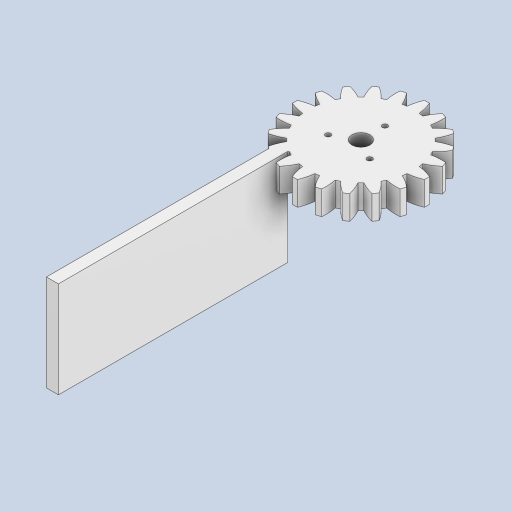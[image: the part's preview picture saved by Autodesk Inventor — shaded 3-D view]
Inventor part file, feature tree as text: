
AUTODESK INVENTOR PART (.ipt)
format: ipt  version: 2023 (Build 270158000, 158)  size: 265,216 bytes
history: native  units: mm (DEFAULTED — no unit token found)
features: sketch x5, extrude x4, plane x3, other x3
ambient origin geometry x8: Origin, YZ Plane, XZ Plane, XY Plane, X Axis, Y Axis, Z Axis, Center Point
bodies: Solid1 (feature_tree)
feature tree (15):
  extrude  "Extrusion1"  Depth=10.0mm TaperAngle=0.0deg
  plane  "Work Plane2"
  plane  "Work Plane8"
  plane  "Work Plane9"
  other  "平歯車"
  extrude  "押し出し2"  Depth=10.0mm TaperAngle=0.0deg
  extrude  "押し出し4"  Depth=0.5mm
  extrude  "押し出し6"  Depth=0.5mm TaperAngle=0.0deg
  sketch  "Sketch1"  dims[d0=55.0mm d1=10.0mm d2=0.0mm]
  sketch  "Sketch2"  dims[d3=50.0mm d4=10.0mm d5=0.0mm d16=50.0mm d17=0.0mm d34=1.570796mm d39=0.0mm d41=0.0mm d43=50.0mm d46=50.0mm d47=0.0mm d48=0.0mm d52=7.5mm d57=20.0mm d58=0.0mm d59=10.0mm d60=300.0deg d61=2.2mm d62=30.0mm d64=360.0deg d76=5.0mm d77=100.0mm d78=40.0mm d79=0.0mm d85=5.1mm d86=30.0mm d88=360.0deg d90=0.5mm d91=0.0mm]
  other  "Srf1"
  sketch  "スケッチ4"
  sketch  "スケッチ7"
  sketch  "スケッチ9"
  other  "ピッチ円直径"
